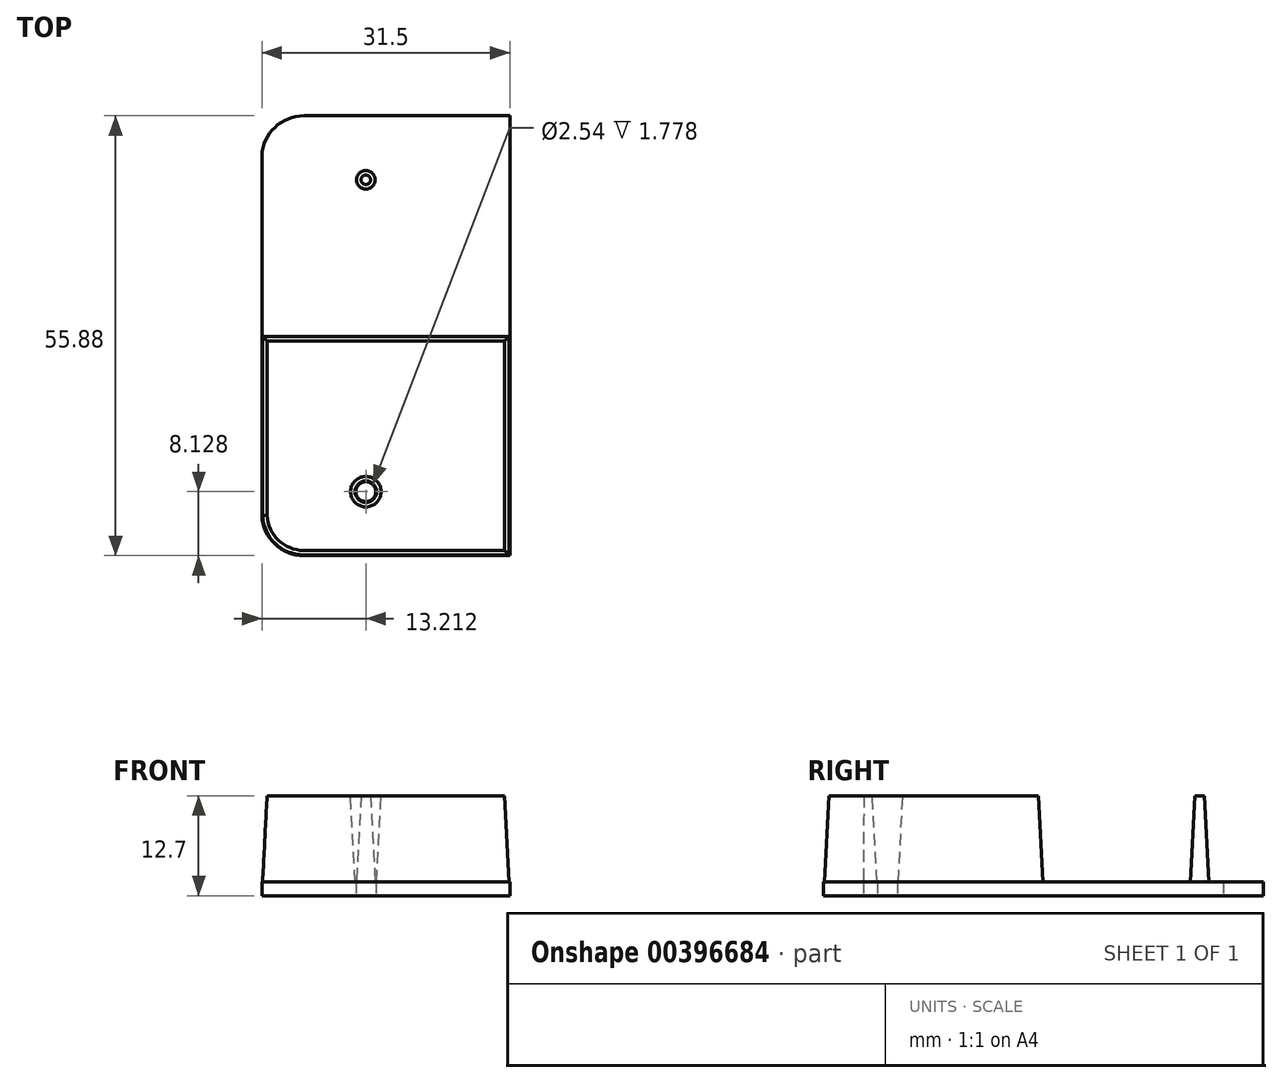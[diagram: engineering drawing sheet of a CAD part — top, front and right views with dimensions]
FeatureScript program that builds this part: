
annotation { "Feature Type Name" : "Feature", "Feature Type Description" : "" }
export const myFeature = defineFeature(function(context is Context, id is Id, definition is map)
    precondition{}
    {
        {
            var Q0;
            Q0=qCreatedBy(makeId("Top.planeOp"),FACE);
            var sketch = newSketch(context, id + "F0", { "sketchPlane" : qUnion([Q0])});
            skLineSegment(sketch, "E0", {"start": v(0, 0) * mm, "end": v(0, 55.88) * mm});
            skLineSegment(sketch, "E1", {"start": v(0, 55.88) * mm, "end": v(0, 50.8) * mm});
            skLineSegment(sketch, "E2", {"start": v(0, 27.94) * mm, "end": v(-59.74, 27.94) * mm});
            skLineSegment(sketch, "E3", {"start": v(0, 55.88) * mm, "end": v(-26.16, 55.88) * mm});
            skArc(sketch, "E4", {"start": v(-26.16, 55.88) * mm, "mid": v(-29.85, 54.4) * mm, "end": v(-31.5, 50.8) * mm});
            skLineSegment(sketch, "E5", {"start": v(0, 55.88) * mm, "end": v(-18.29, 55.88) * mm});
            skLineSegment(sketch, "E6", {"start": v(-18.29, 55.88) * mm, "end": v(-18.29, 47.75) * mm});
            skCircle(sketch, "E7", {"center": v(-18.29, 47.75) * mm, "radius": 1.27 * mm});
            skLineSegment(sketch, "E8.MirrorCS", {"start": v(0, 0) * mm, "end": v(0, 5.08) * mm});
            skLineSegment(sketch, "E9.MirrorCS", {"start": v(0, 0) * mm, "end": v(-18.29, 0) * mm});
            skLineSegment(sketch, "E10.MirrorCS", {"start": v(-18.29, 0) * mm, "end": v(-18.29, 8.13) * mm});
            skCircle(sketch, "E11.MirrorC", {"center": v(-18.29, 8.13) * mm, "radius": 1.27 * mm});
            skArc(sketch, "E12.MirrorCS", {"start": v(-26.16, 0) * mm, "mid": v(-29.85, 1.47) * mm, "end": v(-31.5, 5.08) * mm});
            skLineSegment(sketch, "E13.MirrorCS", {"start": v(0, 0) * mm, "end": v(-26.16, 0) * mm});
            skLineSegment(sketch, "E14", {"start": v(-31.5, 50.8) * mm, "end": v(-31.5, 5.08) * mm});
            skSolve(sketch);
        }
        {
            var Q0;
            Q0 = qSketchRegion(id + "F0", true);
            var Q1;
            Q1=makeQuery(id+"F0.imprint","IMPRINT",FACE,{"disambiguationData":[TD([[makeQuery(id+"F0.imprint","IMPRINT",EDGE,{"derivedFrom":sQuery(id+"F0.wireOp",EDGE,"E7")}),1.0]])]});
            var Q2;
            Q2=makeQuery(id+"F0.imprint","IMPRINT",FACE,{"disambiguationData":[TD([[makeQuery(id+"F0.imprint","IMPRINT",EDGE,{"derivedFrom":sQuery(id+"F0.wireOp",EDGE,"E11.MirrorC")}),-1.0]])]});
            extrude(context, id + "F1", {"entities" : qUnion([Q0, Q1, Q2]), "depth" : 1.78 * mm});
        }
        {
            var Q0;
            Q0=makeQuery(id+"F0.imprint","IMPRINT",FACE,{"disambiguationData":[TD([[makeQuery(id+"F0.imprint","IMPRINT",EDGE,{"derivedFrom":sQuery(id+"F0.wireOp",EDGE,"E7")}),1.0]])]});
            var Q1;
            Q1=makeQuery(id+"F0.imprint","IMPRINT",FACE,{"disambiguationData":[TD([[makeQuery(id+"F0.imprint","IMPRINT",EDGE,{"derivedFrom":sQuery(id+"F0.wireOp",EDGE,"E11.MirrorC")}),-1.0]])]});
            extrude(context, id + "F2", {"entities" : qUnion([Q0, Q1]), "operationType" : NewBodyOperationType.ADD, "depth" : 12.7 * mm, "hasDraft" : true, "draftAngle" : 3 * degree, "draftPullDirection" : true});
        }
    });
